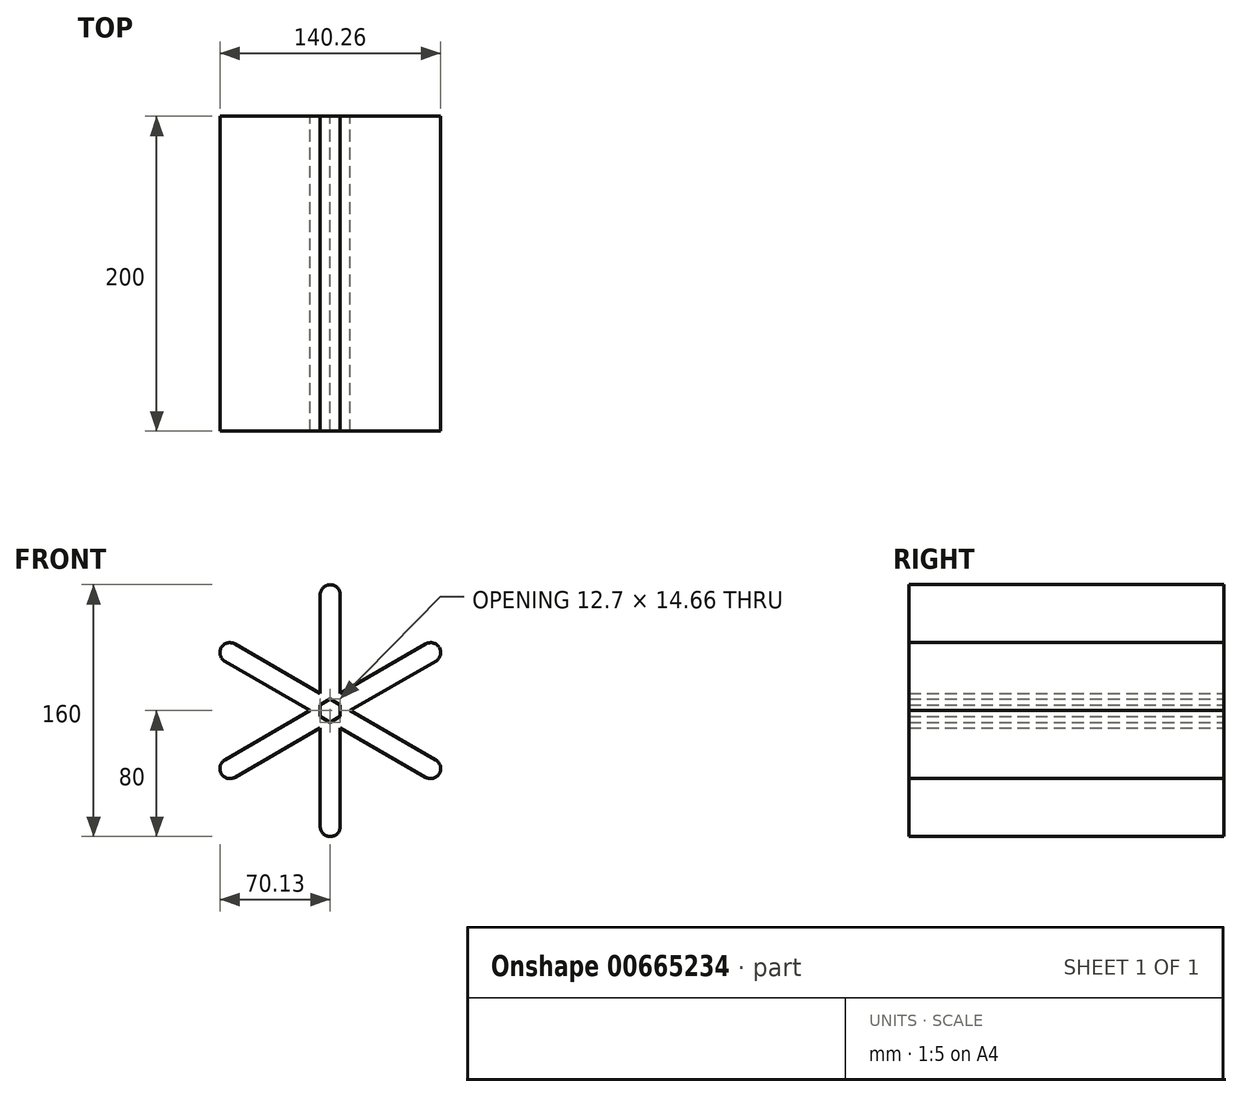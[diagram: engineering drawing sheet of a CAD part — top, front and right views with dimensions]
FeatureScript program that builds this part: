
annotation { "Feature Type Name" : "Feature", "Feature Type Description" : "" }
export const myFeature = defineFeature(function(context is Context, id is Id, definition is map)
    precondition{}
    {
        {
            var Q0;
            Q0=qCreatedBy(makeId("Front.planeOp"),FACE);
            var sketch = newSketch(context, id + "F0", { "sketchPlane" : qUnion([Q0])});
            skLineSegment(sketch, "E0", {"start": v(0, 0) * mm, "end": v(0, -73.65) * mm});
            skLineSegment(sketch, "E1", {"start": v(0, 0) * mm, "end": v(0, 73.65) * mm});
            skLineSegment(sketch, "E2", {"start": v(0, 0) * mm, "end": v(-63.78, -36.82) * mm});
            skLineSegment(sketch, "E3", {"start": v(0, 0) * mm, "end": v(63.78, -36.82) * mm});
            skLineSegment(sketch, "E4", {"start": v(0, 0) * mm, "end": v(-63.78, 36.83) * mm});
            skLineSegment(sketch, "E5", {"start": v(0, 0) * mm, "end": v(63.78, 36.83) * mm});
            skArc(sketch, "E6.0.startCap", {"start": v(3.17, -5.5) * mm, "mid": v(-5.5, -3.18) * mm, "end": v(-3.18, 5.5) * mm});
            skArc(sketch, "E6.0.endCap", {"start": v(60.6, 42.32) * mm, "mid": v(69.28, 40) * mm, "end": v(66.96, 31.33) * mm});
            skLineSegment(sketch, "E6.0.left", {"start": v(-3.18, 5.5) * mm, "end": v(60.6, 42.32) * mm});
            skLineSegment(sketch, "E6.0.right", {"start": v(3.17, -5.5) * mm, "end": v(66.96, 31.33) * mm});
            skArc(sketch, "E7.0.startCap", {"start": v(6.35, 0) * mm, "mid": v(0, -6.35) * mm, "end": v(-6.35, 0) * mm});
            skArc(sketch, "E7.0.endCap", {"start": v(-6.35, 73.65) * mm, "mid": v(0, 80) * mm, "end": v(6.35, 73.65) * mm});
            skLineSegment(sketch, "E7.0.left", {"start": v(-6.35, 0) * mm, "end": v(-6.35, 73.65) * mm});
            skLineSegment(sketch, "E7.0.right", {"start": v(6.35, 0) * mm, "end": v(6.35, 73.65) * mm});
            skArc(sketch, "E7.1.startCap", {"start": v(3.18, 5.5) * mm, "mid": v(5.5, -3.18) * mm, "end": v(-3.17, -5.5) * mm});
            skArc(sketch, "E7.1.endCap", {"start": v(-66.96, 31.33) * mm, "mid": v(-69.28, 40) * mm, "end": v(-60.6, 42.32) * mm});
            skLineSegment(sketch, "E7.1.left", {"start": v(-3.17, -5.5) * mm, "end": v(-66.96, 31.33) * mm});
            skLineSegment(sketch, "E7.1.right", {"start": v(3.18, 5.5) * mm, "end": v(-60.6, 42.32) * mm});
            skArc(sketch, "E7.2.startCap", {"start": v(-3.18, 5.5) * mm, "mid": v(5.5, 3.17) * mm, "end": v(3.17, -5.5) * mm});
            skArc(sketch, "E7.2.endCap", {"start": v(-60.6, -42.32) * mm, "mid": v(-69.28, -40) * mm, "end": v(-66.96, -31.33) * mm});
            skLineSegment(sketch, "E7.2.left", {"start": v(3.17, -5.5) * mm, "end": v(-60.6, -42.32) * mm});
            skLineSegment(sketch, "E7.2.right", {"start": v(-3.18, 5.5) * mm, "end": v(-66.96, -31.33) * mm});
            skArc(sketch, "E7.3.startCap", {"start": v(-6.35, 0) * mm, "mid": v(0, 6.35) * mm, "end": v(6.35, 0) * mm});
            skArc(sketch, "E7.3.endCap", {"start": v(6.35, -73.65) * mm, "mid": v(0, -80) * mm, "end": v(-6.35, -73.65) * mm});
            skLineSegment(sketch, "E7.3.left", {"start": v(6.35, 0) * mm, "end": v(6.35, -73.65) * mm});
            skLineSegment(sketch, "E7.3.right", {"start": v(-6.35, 0) * mm, "end": v(-6.35, -73.65) * mm});
            skArc(sketch, "E8.0.startCap", {"start": v(-3.18, -5.5) * mm, "mid": v(-5.5, 3.18) * mm, "end": v(3.17, 5.5) * mm});
            skArc(sketch, "E8.0.endCap", {"start": v(66.96, -31.33) * mm, "mid": v(69.28, -40) * mm, "end": v(60.6, -42.32) * mm});
            skLineSegment(sketch, "E8.0.left", {"start": v(3.17, 5.5) * mm, "end": v(66.96, -31.33) * mm});
            skLineSegment(sketch, "E8.0.right", {"start": v(-3.18, -5.5) * mm, "end": v(60.6, -42.32) * mm});
            skSolve(sketch);
        }
        {
            var Q0;
            Q0=qSketchRegion(id+"F0",true);
            extrude(context, id + "F1", {"entities" : qUnion([Q0]), "depth" : 200 * mm});
        }
    });
